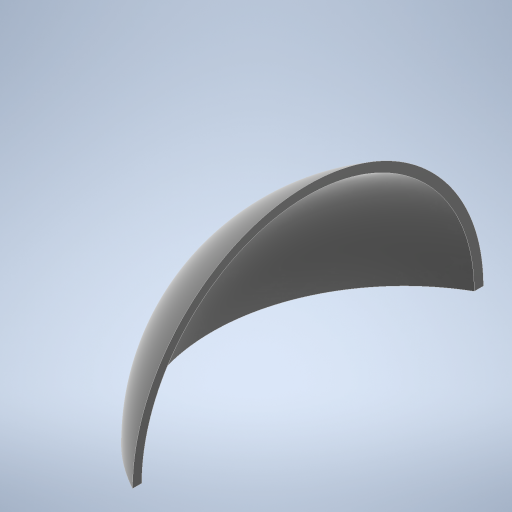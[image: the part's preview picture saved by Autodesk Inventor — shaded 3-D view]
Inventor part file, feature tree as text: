
AUTODESK INVENTOR PART (.ipt)
format: ipt  version: 2023 (Build 270158000, 158)  size: 265,728 bytes
history: native  units: mm
features: sketch x3, revolve x2, other x1, extrude x1
ambient origin geometry x8: Origin, YZ Plane, XZ Plane, XY Plane, X Axis, Y Axis, Z Axis, Center Point
bodies: Body1 (feature_tree)
feature tree (7):
  other  "ソリッド1"
  revolve  "回転1"
  extrude  "押し出し1"  Depth=125.0mm
  revolve  "回転2"
  sketch  "スケッチ1"
  sketch  "スケッチ2"
  sketch  "スケッチ3"
